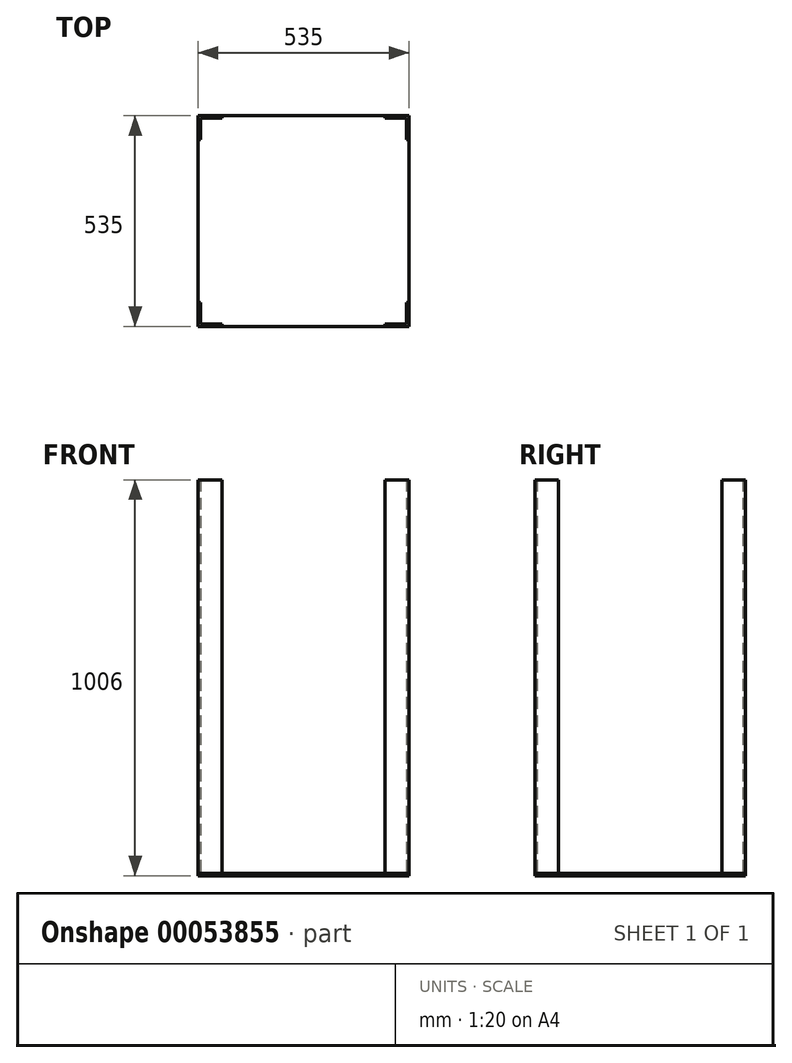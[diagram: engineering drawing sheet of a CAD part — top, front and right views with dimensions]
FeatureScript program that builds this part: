
annotation { "Feature Type Name" : "Feature", "Feature Type Description" : "" }
export const myFeature = defineFeature(function(context is Context, id is Id, definition is map)
    precondition{}
    {
        {
            var Q0;
            Q0=qCreatedBy(makeId("Top.planeOp"),FACE);
            var sketch = newSketch(context, id + "F0", { "sketchPlane" : qUnion([Q0])});
            skLineSegment(sketch, "E0.bottom", {"start": v(0, 0) * mm, "end": v(535, 0) * mm});
            skLineSegment(sketch, "E0.top", {"start": v(0, 535) * mm, "end": v(535, 535) * mm});
            skLineSegment(sketch, "E0.left", {"start": v(0, 0) * mm, "end": v(0, 535) * mm});
            skLineSegment(sketch, "E0.right", {"start": v(535, 0) * mm, "end": v(535, 535) * mm});
            skLineSegment(sketch, "E1", {"start": v(0, 60) * mm, "end": v(6, 60) * mm});
            skLineSegment(sketch, "E2", {"start": v(6, 60) * mm, "end": v(6, 6) * mm});
            skLineSegment(sketch, "E3", {"start": v(6, 6) * mm, "end": v(60, 6) * mm});
            skLineSegment(sketch, "E4", {"start": v(60, 6) * mm, "end": v(60, 0) * mm});
            skLineSegment(sketch, "E5", {"start": v(60, 0) * mm, "end": v(0, 0) * mm});
            skLineSegment(sketch, "E6", {"start": v(0, 60) * mm, "end": v(0, 0) * mm});
            skLineSegment(sketch, "E7", {"start": v(535, 60) * mm, "end": v(529, 60) * mm});
            skLineSegment(sketch, "E8", {"start": v(529, 60) * mm, "end": v(529, 6) * mm});
            skLineSegment(sketch, "E9", {"start": v(529, 6) * mm, "end": v(475, 6) * mm});
            skLineSegment(sketch, "E10", {"start": v(475, 6) * mm, "end": v(475, 0) * mm});
            skLineSegment(sketch, "E11", {"start": v(475, 0) * mm, "end": v(535, 0) * mm});
            skLineSegment(sketch, "E12", {"start": v(60, 535) * mm, "end": v(60, 529) * mm});
            skLineSegment(sketch, "E13", {"start": v(60, 529) * mm, "end": v(6, 529) * mm});
            skLineSegment(sketch, "E14", {"start": v(6, 529) * mm, "end": v(6, 475) * mm});
            skLineSegment(sketch, "E15", {"start": v(6, 475) * mm, "end": v(0, 475) * mm});
            skLineSegment(sketch, "E16", {"start": v(475, 535) * mm, "end": v(475, 529) * mm});
            skLineSegment(sketch, "E17", {"start": v(475, 529) * mm, "end": v(529, 529) * mm});
            skLineSegment(sketch, "E18", {"start": v(529, 529) * mm, "end": v(529, 475) * mm});
            skLineSegment(sketch, "E19", {"start": v(529, 475) * mm, "end": v(535, 475) * mm});
            skSolve(sketch);
        }
        {
            var Q0;
            {var subQ3=sQuery(id+"F0.wireOp",EDGE,"E12");Q0=makeQuery(id+"F0.imprint","IMPRINT",FACE,{"disambiguationData":[TD([[makeQuery(id+"F0.imprint","IMPRINT",EDGE,{"derivedFrom":subQ3}),-1.0]])]});}
            var Q1;
            {var subQ0=sQuery(id+"F0.wireOp",EDGE,"E16");Q1=makeQuery(id+"F0.imprint","IMPRINT",FACE,{"disambiguationData":[TD([[makeQuery(id+"F0.imprint","IMPRINT",EDGE,{"derivedFrom":subQ0}),1.0]])]});}
            var Q2;
            {var subQ2=sQuery(id+"F0.wireOp",EDGE,"E7");Q2=makeQuery(id+"F0.imprint","IMPRINT",FACE,{"disambiguationData":[TD([[makeQuery(id+"F0.imprint","IMPRINT",EDGE,{"derivedFrom":subQ2}),1.0]])]});}
            var Q3;
            Q3=makeQuery(id+"F0.imprint","IMPRINT",FACE,{"disambiguationData":[TD([[makeQuery(id+"F0.imprint","IMPRINT",EDGE,{"derivedFrom":sQuery(id+"F0.wireOp",EDGE,"E1")}),-1.0]])]});
            extrude(context, id + "F1", {"entities" : qUnion([Q0, Q1, Q2, Q3]), "depth" : 1000 * mm});
        }
        {
            var Q0;
            Q0 = qSketchRegion(id + "F0", true);
            extrude(context, id + "F2", {"entities" : qUnion([Q0]), "oppositeDirection" : true, "depth" : 6 * mm});
        }
    });
